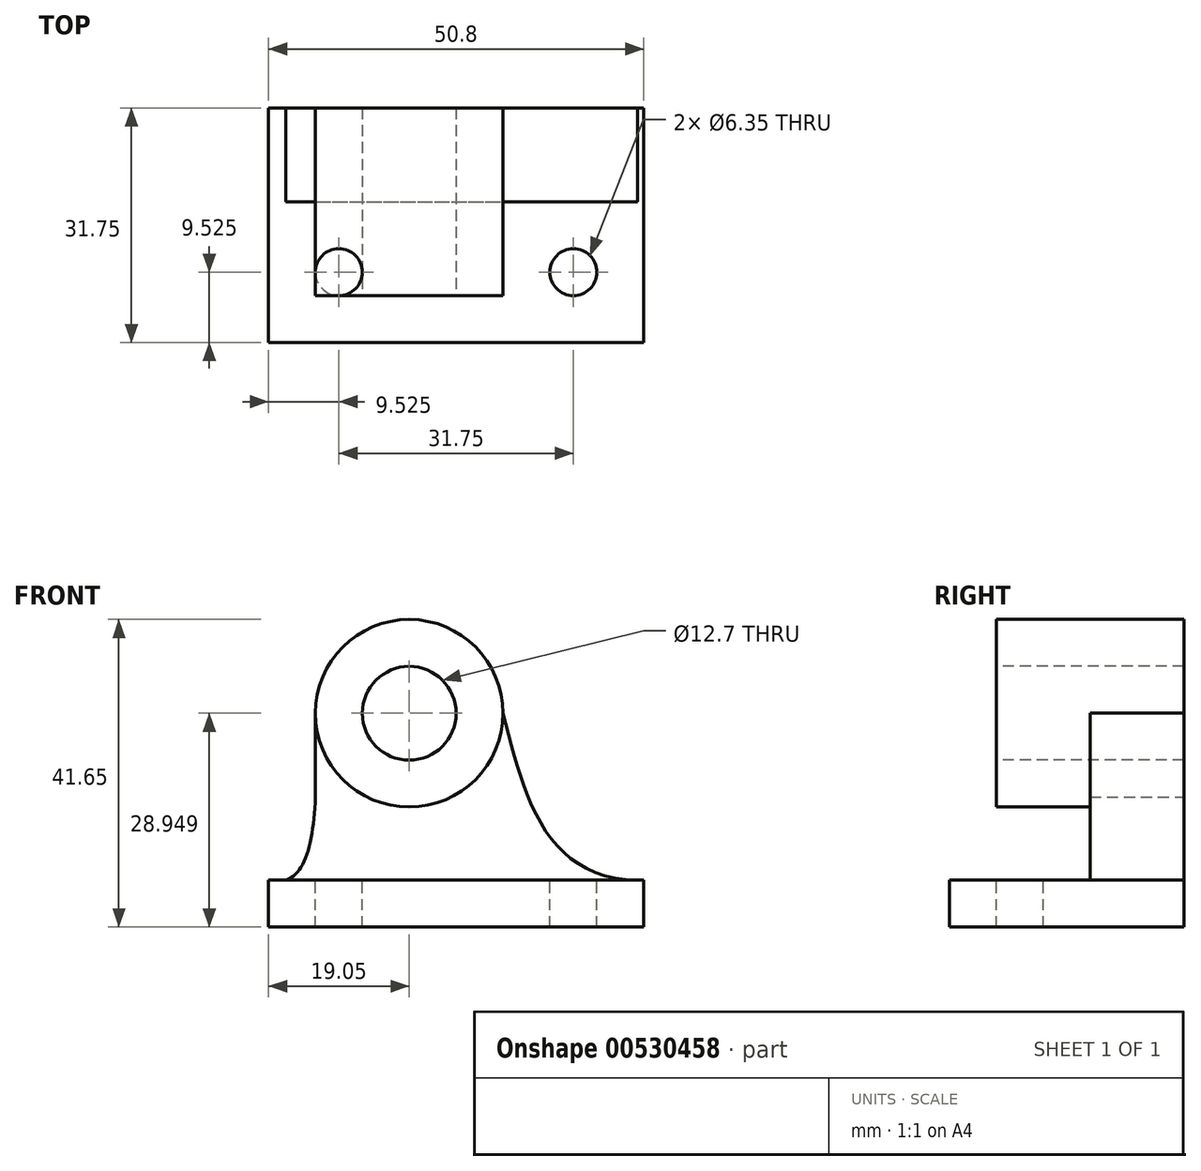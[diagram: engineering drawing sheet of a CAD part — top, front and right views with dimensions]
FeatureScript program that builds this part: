
annotation { "Feature Type Name" : "Feature", "Feature Type Description" : "" }
export const myFeature = defineFeature(function(context is Context, id is Id, definition is map)
    precondition{}
    {
        {
            var Q0;
            Q0=qCreatedBy(makeId("Front.planeOp"),FACE);
            var sketch = newSketch(context, id + "F0", { "sketchPlane" : qUnion([Q0])});
            skLineSegment(sketch, "E0", {"start": v(-68.66, 60.23) * mm, "end": v(-43.26, 60.23) * mm});
            skLineSegment(sketch, "E1", {"start": v(-43.26, 60.23) * mm, "end": v(-43.26, 24.93) * mm});
            skLineSegment(sketch, "E2", {"start": v(-43.26, 24.93) * mm, "end": v(-24.2, 24.93) * mm});
            skLineSegment(sketch, "E3", {"start": v(-24.2, 24.93) * mm, "end": v(-24.2, 18.58) * mm});
            skLineSegment(sketch, "E4", {"start": v(-24.2, 18.58) * mm, "end": v(-75, 18.58) * mm});
            skLineSegment(sketch, "E5", {"start": v(-75, 18.58) * mm, "end": v(-75, 24.93) * mm});
            skLineSegment(sketch, "E6", {"start": v(-75, 24.93) * mm, "end": v(-68.66, 24.93) * mm});
            skLineSegment(sketch, "E7", {"start": v(-68.66, 24.93) * mm, "end": v(-68.66, 60.23) * mm});
            skCircle(sketch, "E8", {"center": v(-55.96, 47.53) * mm, "radius": 12.7 * mm});
            skFitSpline(sketch, "E9", {"points": [v(-43.26, 47.53) * mm, v(-24.2, 24.93) * mm, v(58.69, 65.7) * mm, v(58.88, 66.08) * mm], "startDerivative": vector(24.94, -99) * mm, "endDerivative": vector(-1.27, 5.47) * mm});
            skFitSpline(sketch, "E10", {"points": [v(-68.66, 47.53) * mm, v(-75, 24.93) * mm, v(-132.65, 71.27) * mm, v(-138.22, 57.05) * mm, v(-138.4, 57.25) * mm], "startDerivative": vector(2.75, -134.64) * mm, "endDerivative": vector(-6.78, 13.6) * mm});
            skSolve(sketch);
        }
        {
            var Q0;
            {var subQ0=sQuery(id+"F0.wireOp",EDGE,"E2");var subQ1=sQuery(id+"F0.wireOp",EDGE,"E1");var subQ2=makeQuery(id+"F0.imprint","INTERSECT",VERTEX,{"derivedFrom":[subQ1,subQ0]});Q0=makeQuery(id+"F0.imprint","IMPRINT",FACE,{"disambiguationData":[TD([[makeQuery(id+"F0.imprint","IMPRINT",EDGE,{"disambiguationData":[TD([[subQ2,-1.0]])],"derivedFrom":subQ0}),1.0]])]});}
            var Q1;
            {var subQ0=sQuery(id+"F0.wireOp",EDGE,"E9");var subQ1=sQuery(id+"F0.wireOp",EDGE,"E2");var subQ3=makeQuery(id+"F0.imprint","INTERSECT",VERTEX,{"derivedFrom":[subQ1,subQ0]});Q1=makeQuery(id+"F0.imprint","IMPRINT",FACE,{"disambiguationData":[TD([[makeQuery(id+"F0.imprint","IMPRINT",EDGE,{"disambiguationData":[TD([[subQ3,-1.0]])],"derivedFrom":subQ1}),-1.0]])]});}
            var Q2;
            {var subQ0=sQuery(id+"F0.wireOp",EDGE,"E10");var subQ1=sQuery(id+"F0.wireOp",EDGE,"E6");var subQ3=makeQuery(id+"F0.imprint","INTERSECT",VERTEX,{"derivedFrom":[subQ1,subQ0]});Q2=makeQuery(id+"F0.imprint","IMPRINT",FACE,{"disambiguationData":[TD([[makeQuery(id+"F0.imprint","IMPRINT",EDGE,{"disambiguationData":[TD([[subQ3,1.0]])],"derivedFrom":subQ1}),-1.0]])]});}
            var Q3;
            {var subQ0=sQuery(id+"F0.wireOp",EDGE,"E7");var subQ1=sQuery(id+"F0.wireOp",EDGE,"E6");var subQ2=makeQuery(id+"F0.imprint","INTERSECT",VERTEX,{"derivedFrom":[subQ1,subQ0]});Q3=makeQuery(id+"F0.imprint","IMPRINT",FACE,{"disambiguationData":[TD([[makeQuery(id+"F0.imprint","IMPRINT",EDGE,{"disambiguationData":[TD([[subQ2,1.0]])],"derivedFrom":subQ1}),1.0]])]});}
            var Q4;
            {var subQ0=sQuery(id+"F0.wireOp",EDGE,"E10");var subQ2=sQuery(id+"F0.wireOp",EDGE,"E7");var subQ4=makeQuery(id+"F0.imprint","INTERSECT",VERTEX,{"derivedFrom":[subQ2,subQ0]});Q4=makeQuery(id+"F0.imprint","IMPRINT",FACE,{"disambiguationData":[TD([[makeQuery(id+"F0.imprint","IMPRINT",EDGE,{"disambiguationData":[TD([[subQ4,1.0]])],"derivedFrom":subQ0}),-1.0]])]});}
            var Q5;
            {var subQ0=sQuery(id+"F0.wireOp",EDGE,"E10");var subQ1=sQuery(id+"F0.wireOp",EDGE,"E8");var subQ3=makeQuery(id+"F0.imprint","INTERSECT",VERTEX,{"derivedFrom":[subQ1,subQ0]});Q5=makeQuery(id+"F0.imprint","IMPRINT",FACE,{"disambiguationData":[TD([[makeQuery(id+"F0.imprint","IMPRINT",EDGE,{"disambiguationData":[TD([[subQ3,1.0]])],"derivedFrom":subQ1}),1.0]])]});}
            var Q6;
            {var subQ9=sQuery(id+"F0.wireOp",EDGE,"E3");Q6=makeQuery(id+"F0.imprint","IMPRINT",FACE,{"disambiguationData":[TD([[makeQuery(id+"F0.imprint","IMPRINT",EDGE,{"derivedFrom":subQ9}),-1.0]])]});}
            var Q7;
            {var subQ0=sQuery(id+"F0.wireOp",EDGE,"E8");var subQ2=makeQuery(id+"F0.imprint","INTERSECT",VERTEX,{"derivedFrom":[sQuery(id+"F0.wireOp",EDGE,"E0"),subQ0]});Q7=makeQuery(id+"F0.imprint","IMPRINT",FACE,{"disambiguationData":[TD([[makeQuery(id+"F0.imprint","IMPRINT",EDGE,{"disambiguationData":[TD([[subQ2,1.0]])],"derivedFrom":subQ0}),1.0]])]});}
            extrude(context, id + "F1", {"entities" : qUnion([Q0, Q1, Q2, Q3, Q4, Q5, Q6, Q7]), "depth" : 25.4 * mm, "offsetDistance" : 25.4 * mm});
        }
        {
            var Q0;
            Q0=makeQuery(id+"F1.opExtrude","CAP_FACE",FACE,{"disambiguationData":[OSD([sQuery(id+"F0.wireOp",EDGE,"E2"),sQuery(id+"F0.wireOp",EDGE,"E3"),sQuery(id+"F0.wireOp",EDGE,"E4"),sQuery(id+"F0.wireOp",EDGE,"E5"),sQuery(id+"F0.wireOp",EDGE,"E6"),sQuery(id+"F0.wireOp",EDGE,"E7"),sQuery(id+"F0.wireOp",EDGE,"E8"),sQuery(id+"F0.wireOp",EDGE,"E9"),sQuery(id+"F0.wireOp",EDGE,"E10")])],"isStart":false});
            var sketch = newSketch(context, id + "F2", { "sketchPlane" : qUnion([Q0])});
            skCircle(sketch, "E11", {"center": v(-55.96, 47.53) * mm, "radius": 12.7 * mm});
            skSolve(sketch);
        }
        {
            var Q0;
            Q0=makeQuery(id+"F2.imprint","IMPRINT",FACE,{"disambiguationData":[TD([[makeQuery(id+"F2.imprint","IMPRINT",EDGE,{"derivedFrom":makeQuery(id+"F1.opExtrude","CAP_EDGE",EDGE,{"disambiguationData":[OSD([sQuery(id+"F0.wireOp",EDGE,"E2")])],"isStart":false})}),-1.0]])]});
            extrude(context, id + "F3", {"entities" : qUnion([Q0]), "operationType" : NewBodyOperationType.ADD, "depth" : 6.35 * mm, "offsetDistance" : 25.4 * mm});
        }
        {
            var Q0;
            Q0=makeQuery(id+"F3.opExtrude","CAP_FACE",FACE,{"disambiguationData":[OSD([sQuery(id+"F0.wireOp",EDGE,"E2"),sQuery(id+"F0.wireOp",EDGE,"E3"),sQuery(id+"F0.wireOp",EDGE,"E4"),sQuery(id+"F0.wireOp",EDGE,"E5"),sQuery(id+"F0.wireOp",EDGE,"E6"),sQuery(id+"F0.wireOp",EDGE,"E7"),sQuery(id+"F0.wireOp",EDGE,"E9"),sQuery(id+"F0.wireOp",EDGE,"E10"),sQuery(id+"F2.wireOp",EDGE,"E11")])],"isStart":false});
            var sketch = newSketch(context, id + "F4", { "sketchPlane" : qUnion([Q0])});
            skLineSegment(sketch, "E12", {"start": v(-75, 24.93) * mm, "end": v(-24.2, 24.93) * mm});
            skSolve(sketch);
        }
        {
            var Q0;
            Q0 = qSketchRegion(id + "F4", true);
            var Q1;
            Q1=makeQuery(id+"F4.imprint","IMPRINT",FACE,{"disambiguationData":[TD([[makeQuery(id+"F4.imprint","IMPRINT",EDGE,{"derivedFrom":makeQuery(id+"F3.opExtrude","CAP_EDGE",EDGE,{"disambiguationData":[OSD([sQuery(id+"F2.wireOp",EDGE,"E11")])],"isStart":false})}),-1.0]])]});
            extrude(context, id + "F5", {"entities" : qUnion([Q0, Q1]), "operationType" : NewBodyOperationType.REMOVE, "oppositeDirection" : true, "depth" : 19.05 * mm, "offsetDistance" : 25.4 * mm});
        }
        {
            var Q0;
            Q0=makeQuery(id+"F1.opExtrude","CAP_FACE",FACE,{"disambiguationData":[OSD([sQuery(id+"F0.wireOp",EDGE,"E2"),sQuery(id+"F0.wireOp",EDGE,"E3"),sQuery(id+"F0.wireOp",EDGE,"E4"),sQuery(id+"F0.wireOp",EDGE,"E5"),sQuery(id+"F0.wireOp",EDGE,"E6"),sQuery(id+"F0.wireOp",EDGE,"E7"),sQuery(id+"F0.wireOp",EDGE,"E8"),sQuery(id+"F0.wireOp",EDGE,"E9"),sQuery(id+"F0.wireOp",EDGE,"E10")])],"isStart":false});
            var sketch = newSketch(context, id + "F6", { "sketchPlane" : qUnion([Q0])});
            skCircle(sketch, "E13", {"center": v(-55.96, 47.53) * mm, "radius": 6.35 * mm});
            skSolve(sketch);
        }
        {
            var Q0;
            Q0=makeQuery(id+"F6.imprint","IMPRINT",FACE,{"disambiguationData":[TD([[makeQuery(id+"F6.imprint","IMPRINT",EDGE,{"derivedFrom":sQuery(id+"F6.wireOp",EDGE,"E13")}),1.0]])]});
            extrude(context, id + "F7", {"entities" : qUnion([Q0]), "operationType" : NewBodyOperationType.REMOVE, "endBound" : BoundingType.THROUGH_ALL, "oppositeDirection" : true, "depth" : 25.4 * mm, "offsetDistance" : 25.4 * mm});
        }
        {
            var Q0;
            {var subQ0=sQuery(id+"F0.wireOp",EDGE,"E6");var subQ1=sQuery(id+"F0.wireOp",EDGE,"E2");Q0=makeQuery(id+"F5.boolean.opBoolean","MERGE",FACE,{"derivedFrom":[makeQuery(id+"F3.boolean.opBoolean","MERGE",FACE,{"derivedFrom":[makeQuery(id+"F1.opExtrude","SWEPT_FACE",FACE,{"disambiguationData":[OSD([subQ1])]}),makeQuery(id+"F3.opExtrude","SWEPT_FACE",FACE,{"disambiguationData":[OSD([subQ1])]})]}),makeQuery(id+"F3.boolean.opBoolean","MERGE",FACE,{"derivedFrom":[makeQuery(id+"F1.opExtrude","SWEPT_FACE",FACE,{"disambiguationData":[OSD([subQ0])]}),makeQuery(id+"F3.opExtrude","SWEPT_FACE",FACE,{"disambiguationData":[OSD([subQ0])]})]}),makeQuery(id+"F5.opExtrude","SWEPT_FACE",FACE,{"disambiguationData":[OSD([sQuery(id+"F4.wireOp",EDGE,"E12")])]})]});}
            var sketch = newSketch(context, id + "F8", { "sketchPlane" : qUnion([Q0])});
            skCircle(sketch, "E14", {"center": v(-65.48, -22.23) * mm, "radius": 3.18 * mm});
            skCircle(sketch, "E15", {"center": v(-33.73, -22.23) * mm, "radius": 3.18 * mm});
            skSolve(sketch);
        }
        {
            var Q0;
            Q0 = qSketchRegion(id + "F8", true);
            extrude(context, id + "F9", {"entities" : qUnion([Q0]), "operationType" : NewBodyOperationType.REMOVE, "endBound" : BoundingType.THROUGH_ALL, "oppositeDirection" : true, "depth" : 25.4 * mm, "offsetDistance" : 25.4 * mm});
        }
    });
